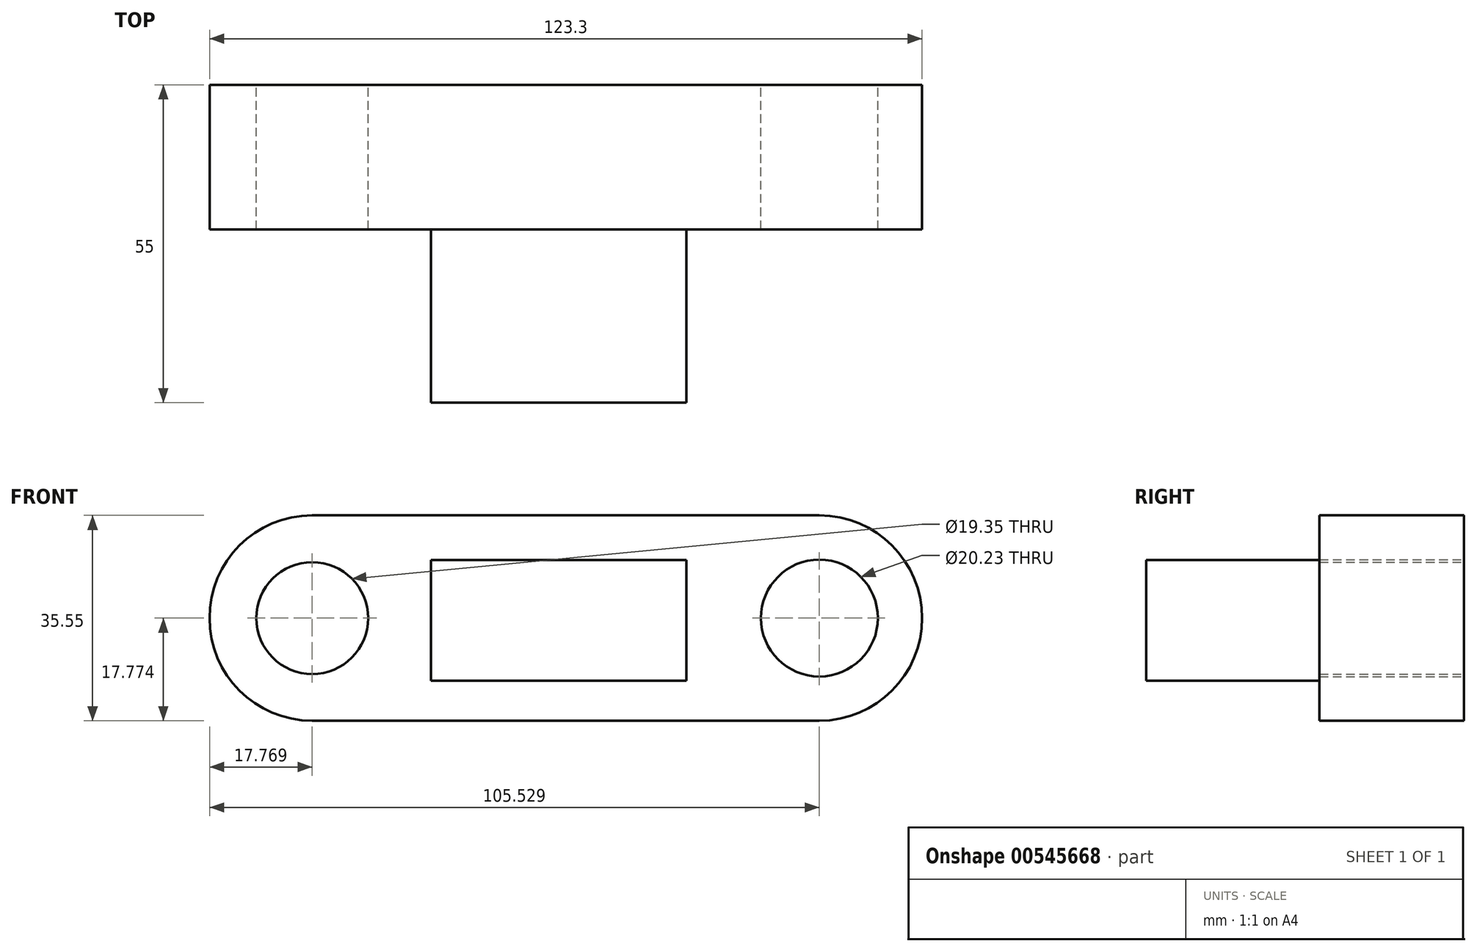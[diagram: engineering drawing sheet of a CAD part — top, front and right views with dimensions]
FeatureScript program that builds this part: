
annotation { "Feature Type Name" : "Feature", "Feature Type Description" : "" }
export const myFeature = defineFeature(function(context is Context, id is Id, definition is map)
    precondition{}
    {
        {
            var Q0;
            Q0=qCreatedBy(makeId("Front.planeOp"),FACE);
            var sketch = newSketch(context, id + "F0", { "sketchPlane" : qUnion([Q0])});
            skLineSegment(sketch, "E0.bottom", {"start": v(-43.66, 19.97) * mm, "end": v(44.1, 19.97) * mm});
            skLineSegment(sketch, "E0.top", {"start": v(-43.66, -15.58) * mm, "end": v(44.1, -15.58) * mm});
            skArc(sketch, "E1", {"start": v(-43.66, 19.97) * mm, "mid": v(-61.43, 2.2) * mm, "end": v(-43.66, -15.58) * mm});
            skArc(sketch, "E2", {"start": v(44.1, -15.58) * mm, "mid": v(61.87, 2.2) * mm, "end": v(44.1, 19.97) * mm});
            skCircle(sketch, "E3", {"center": v(-43.66, 2.2) * mm, "radius": 9.68 * mm});
            skCircle(sketch, "E4", {"center": v(44.1, 2.2) * mm, "radius": 10.11 * mm});
            skSolve(sketch);
        }
        {
            var Q0;
            Q0=makeQuery(id+"F0.imprint","IMPRINT",FACE,{"disambiguationData":[TD([[makeQuery(id+"F0.imprint","IMPRINT",EDGE,{"derivedFrom":sQuery(id+"F0.wireOp",EDGE,"E0.bottom")}),-1.0]])]});
            extrude(context, id + "F1", {"entities" : qUnion([Q0]), "depth" : 25 * mm, "offsetDistance" : 25 * mm});
        }
        {
            var Q0;
            Q0=qCreatedBy(makeId("Front.planeOp"),FACE);
            var sketch = newSketch(context, id + "F2", { "sketchPlane" : qUnion([Q0])});
            skLineSegment(sketch, "E5.bottom", {"start": v(-23.1, -8.64) * mm, "end": v(21.1, -8.64) * mm});
            skLineSegment(sketch, "E5.top", {"start": v(-23.1, 12.25) * mm, "end": v(21.1, 12.25) * mm});
            skLineSegment(sketch, "E5.left", {"start": v(-23.1, -8.64) * mm, "end": v(-23.1, 12.25) * mm});
            skLineSegment(sketch, "E5.right", {"start": v(21.1, -8.64) * mm, "end": v(21.1, 12.25) * mm});
            skSolve(sketch);
        }
        {
            var Q0;
            Q0 = qSketchRegion(id + "F2", true);
            extrude(context, id + "F3", {"entities" : qUnion([Q0]), "operationType" : NewBodyOperationType.ADD, "depth" : 55 * mm, "offsetDistance" : 25 * mm});
        }
    });
